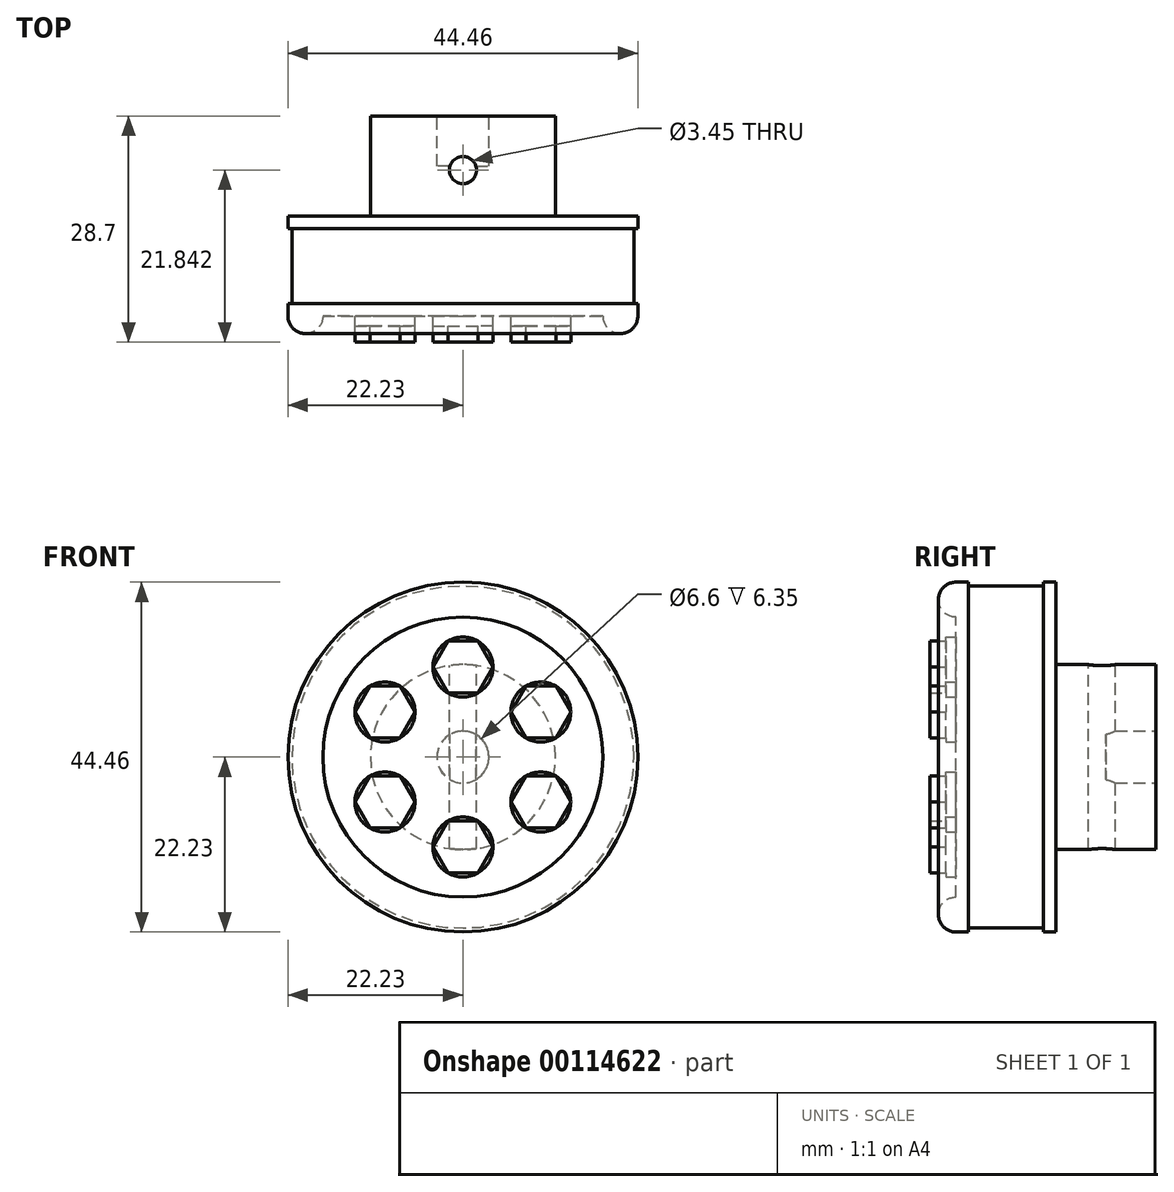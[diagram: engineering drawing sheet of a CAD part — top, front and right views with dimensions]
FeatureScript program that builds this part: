
annotation { "Feature Type Name" : "Feature", "Feature Type Description" : "" }
export const myFeature = defineFeature(function(context is Context, id is Id, definition is map)
    precondition{}
    {
        {
            var Q0;
            Q0=qCreatedBy(makeId("Front.planeOp"),FACE);
            var sketch = newSketch(context, id + "F0", { "sketchPlane" : qUnion([Q0])});
            skCircle(sketch, "E0", {"center": v(0, 0) * mm, "radius": 22.23 * mm});
            skSolve(sketch);
        }
        {
            var Q0;
            Q0 = qSketchRegion(id + "F0", true);
            extrude(context, id + "F1", {"entities" : qUnion([Q0]), "depth" : 12.7 * mm});
        }
        {
            var Q0;
            Q0=makeQuery(id+"F1.opExtrude","CAP_FACE",FACE,{"disambiguationData":[OSD([sQuery(id+"F0.wireOp",EDGE,"E0")])],"isStart":false});
            var sketch = newSketch(context, id + "F2", { "sketchPlane" : qUnion([Q0])});
            skLineSegment(sketch, "E1", {"start": v(0, 0) * mm, "end": v(0, 11.43) * mm, "construction": true});
            skCircle(sketch, "E2", {"center": v(0, 11.43) * mm, "radius": 3.81 * mm});
            skCircle(sketch, "E3.1.0", {"center": v(-9.9, 5.72) * mm, "radius": 3.81 * mm});
            skCircle(sketch, "E3.2.0", {"center": v(-9.9, -5.71) * mm, "radius": 3.81 * mm});
            skPoint(sketch, "E3.center", {"position": v(0, 0) * mm});
            skCircle(sketch, "E4.1.3.0", {"center": v(0, -11.43) * mm, "radius": 3.81 * mm});
            skCircle(sketch, "E4.1.4.0", {"center": v(9.9, -5.72) * mm, "radius": 3.81 * mm});
            skCircle(sketch, "E4.1.5.0", {"center": v(9.9, 5.72) * mm, "radius": 3.81 * mm});
            skLineSegment(sketch, "E5", {"start": v(0, 0) * mm, "end": v(-9.9, 5.72) * mm, "construction": true});
            skLineSegment(sketch, "E6", {"start": v(0, 0) * mm, "end": v(-22.23, 0) * mm, "construction": true});
            skSolve(sketch);
        }
        {
            var Q0;
            Q0 = qSketchRegion(id + "F2", true);
            extrude(context, id + "F3", {"entities" : qUnion([Q0]), "operationType" : NewBodyOperationType.ADD, "depth" : 1.27 * mm});
        }
        {
            var Q0;
            Q0=makeQuery(id+"F3.opExtrude","CAP_FACE",FACE,{"disambiguationData":[OSD([sQuery(id+"F2.wireOp",EDGE,"E2")])],"isStart":false});
            var sketch = newSketch(context, id + "F4", { "sketchPlane" : qUnion([Q0])});
            skLineSegment(sketch, "E7", {"start": v(0, 11.43) * mm, "end": v(3.81, 11.43) * mm, "construction": true});
            skCircle(sketch, "E8.cCircle", {"center": v(0, 11.43) * mm, "radius": 3.81 * mm, "construction": true});
            skLineSegment(sketch, "E8.0", {"start": v(3.81, 11.43) * mm, "end": v(1.9, 8.13) * mm});
            skLineSegment(sketch, "E8.1", {"start": v(1.9, 8.13) * mm, "end": v(-1.9, 8.13) * mm});
            skLineSegment(sketch, "E8.2", {"start": v(-1.9, 8.13) * mm, "end": v(-3.81, 11.43) * mm});
            skLineSegment(sketch, "E8.3", {"start": v(-3.81, 11.43) * mm, "end": v(-1.9, 14.73) * mm});
            skLineSegment(sketch, "E8.4", {"start": v(-1.9, 14.73) * mm, "end": v(1.9, 14.73) * mm});
            skLineSegment(sketch, "E8.5", {"start": v(1.9, 14.73) * mm, "end": v(3.81, 11.43) * mm});
            skLineSegment(sketch, "E9", {"start": v(0, 0) * mm, "end": v(-21.3, 0) * mm, "construction": true});
            skLineSegment(sketch, "E10", {"start": v(0, 0) * mm, "end": v(-9.62, 16.66) * mm, "construction": true});
            skLineSegment(sketch, "E11", {"start": v(0, 0) * mm, "end": v(9.66, 16.73) * mm, "construction": true});
            skLineSegment(sketch, "E12.MirrorCS", {"start": v(-6.09, 5.71) * mm, "end": v(-8, 9.01) * mm});
            skLineSegment(sketch, "E13.MirrorCS", {"start": v(-8, 2.42) * mm, "end": v(-6.09, 5.71) * mm});
            skLineSegment(sketch, "E14.MirrorCS", {"start": v(-11.8, 2.42) * mm, "end": v(-8, 2.42) * mm});
            skLineSegment(sketch, "E15.MirrorCS", {"start": v(-13.7, 5.71) * mm, "end": v(-11.8, 2.42) * mm});
            skLineSegment(sketch, "E16.MirrorCS", {"start": v(-11.8, 9.01) * mm, "end": v(-13.7, 5.71) * mm});
            skLineSegment(sketch, "E17.MirrorCS", {"start": v(-8, 9.01) * mm, "end": v(-11.8, 9.01) * mm});
            skLineSegment(sketch, "E18.MirrorCS", {"start": v(6.09, 5.72) * mm, "end": v(8, 2.42) * mm});
            skLineSegment(sketch, "E19.MirrorCS", {"start": v(8, 9.01) * mm, "end": v(6.09, 5.72) * mm});
            skLineSegment(sketch, "E20.MirrorCS", {"start": v(11.8, 9.01) * mm, "end": v(8, 9.01) * mm});
            skLineSegment(sketch, "E21.MirrorCS", {"start": v(13.7, 5.72) * mm, "end": v(11.8, 9.01) * mm});
            skLineSegment(sketch, "E22.MirrorCS", {"start": v(11.8, 2.42) * mm, "end": v(13.7, 5.72) * mm});
            skLineSegment(sketch, "E23.MirrorCS", {"start": v(8, 2.42) * mm, "end": v(11.8, 2.42) * mm});
            skLineSegment(sketch, "E24.MirrorCS", {"start": v(-11.8, -2.42) * mm, "end": v(-8, -2.42) * mm});
            skLineSegment(sketch, "E25.MirrorCS", {"start": v(-13.7, -5.71) * mm, "end": v(-11.8, -2.42) * mm});
            skLineSegment(sketch, "E26.MirrorCS", {"start": v(-11.8, -9.01) * mm, "end": v(-13.7, -5.71) * mm});
            skLineSegment(sketch, "E27.MirrorCS", {"start": v(-8, -9.01) * mm, "end": v(-11.8, -9.01) * mm});
            skLineSegment(sketch, "E28.MirrorCS", {"start": v(-6.09, -5.71) * mm, "end": v(-8, -9.01) * mm});
            skLineSegment(sketch, "E29.MirrorCS", {"start": v(-8, -2.42) * mm, "end": v(-6.09, -5.71) * mm});
            skLineSegment(sketch, "E30.MirrorCS", {"start": v(1.9, -8.13) * mm, "end": v(-1.9, -8.13) * mm});
            skLineSegment(sketch, "E31.MirrorCS", {"start": v(3.81, -11.43) * mm, "end": v(1.9, -8.13) * mm});
            skLineSegment(sketch, "E32.MirrorCS", {"start": v(1.9, -14.73) * mm, "end": v(3.81, -11.43) * mm});
            skLineSegment(sketch, "E33.MirrorCS", {"start": v(-1.9, -14.73) * mm, "end": v(1.9, -14.73) * mm});
            skLineSegment(sketch, "E34.MirrorCS", {"start": v(-3.81, -11.43) * mm, "end": v(-1.9, -14.73) * mm});
            skLineSegment(sketch, "E35.MirrorCS", {"start": v(-1.9, -8.13) * mm, "end": v(-3.81, -11.43) * mm});
            skLineSegment(sketch, "E36.MirrorCS", {"start": v(6.09, -5.72) * mm, "end": v(8, -2.42) * mm});
            skLineSegment(sketch, "E37.MirrorCS", {"start": v(8, -9.01) * mm, "end": v(6.09, -5.72) * mm});
            skLineSegment(sketch, "E38.MirrorCS", {"start": v(11.8, -9.01) * mm, "end": v(8, -9.01) * mm});
            skLineSegment(sketch, "E39.MirrorCS", {"start": v(13.7, -5.72) * mm, "end": v(11.8, -9.01) * mm});
            skLineSegment(sketch, "E40.MirrorCS", {"start": v(11.8, -2.42) * mm, "end": v(13.7, -5.72) * mm});
            skLineSegment(sketch, "E41.MirrorCS", {"start": v(8, -2.42) * mm, "end": v(11.8, -2.42) * mm});
            skSolve(sketch);
        }
        {
            var Q0;
            Q0 = qSketchRegion(id + "F4", true);
            extrude(context, id + "F5", {"entities" : qUnion([Q0]), "operationType" : NewBodyOperationType.ADD, "depth" : 2.03 * mm});
        }
        {
            var Q0;
            Q0=makeQuery(id+"F1.opExtrude","CAP_FACE",FACE,{"disambiguationData":[OSD([sQuery(id+"F0.wireOp",EDGE,"E0")])],"isStart":false});
            var sketch = newSketch(context, id + "F6", { "sketchPlane" : qUnion([Q0])});
            skCircle(sketch, "E42", {"center": v(0, 0) * mm, "radius": 17.78 * mm});
            skCircle(sketch, "E43", {"center": v(0, 0) * mm, "radius": 22.23 * mm});
            skPoint(sketch, "E44", {"position": v(0, 17.78) * mm});
            skPoint(sketch, "E45", {"position": v(0, 22.23) * mm});
            skSolve(sketch);
        }
        {
            var Q0;
            Q0 = qSketchRegion(id + "F6", true);
            extrude(context, id + "F7", {"entities" : qUnion([Q0]), "operationType" : NewBodyOperationType.ADD, "depth" : 2.22 * mm});
        }
        {
            var Q0;
            Q0=makeQuery(id+"F7.opExtrude","CAP_EDGE",EDGE,{"disambiguationData":[OSD([sQuery(id+"F6.wireOp",EDGE,"E42")])],"isStart":false});
            fillet(context, id + "F8", {"entities" : qUnion([Q0]), "radius" : 2.22 * mm, "tangentPropagation" : true, "allowEdgeOverflow" : false});
        }
        {
            var Q0;
            Q0=makeQuery(id+"F7.opExtrude","CAP_EDGE",EDGE,{"disambiguationData":[OSD([sQuery(id+"F6.wireOp",EDGE,"E43")])],"isStart":false});
            fillet(context, id + "F9", {"entities" : qUnion([Q0]), "radius" : 2.22 * mm, "tangentPropagation" : true, "allowEdgeOverflow" : false});
        }
        {
            var Q0;
            Q0=makeQuery(id+"F1.opExtrude","CAP_FACE",FACE,{"disambiguationData":[OSD([sQuery(id+"F0.wireOp",EDGE,"E0")])],"isStart":true});
            var sketch = newSketch(context, id + "F10", { "sketchPlane" : qUnion([Q0])});
            skCircle(sketch, "E46", {"center": v(0, 0) * mm, "radius": 11.75 * mm});
            skSolve(sketch);
        }
        {
            var Q0;
            Q0 = qSketchRegion(id + "F10", true);
            extrude(context, id + "F11", {"entities" : qUnion([Q0]), "operationType" : NewBodyOperationType.ADD, "depth" : 12.7 * mm});
        }
        {
            var Q0;
            Q0=makeQuery(id+"F11.opExtrude","CAP_FACE",FACE,{"disambiguationData":[OSD([sQuery(id+"F10.wireOp",EDGE,"E46")])],"isStart":false});
            var sketch = newSketch(context, id + "F12", { "sketchPlane" : qUnion([Q0])});
            skCircle(sketch, "E47", {"center": v(0, 0) * mm, "radius": 3.3 * mm});
            skSolve(sketch);
        }
        {
            var Q0;
            Q0 = qSketchRegion(id + "F12", true);
            extrude(context, id + "F13", {"entities" : qUnion([Q0]), "operationType" : NewBodyOperationType.REMOVE, "oppositeDirection" : true, "depth" : 6.35 * mm});
        }
        {
            var Q0;
            Q0=qCreatedBy(makeId("Top.planeOp"),FACE);
            var sketch = newSketch(context, id + "F14", { "sketchPlane" : qUnion([Q0])});
            skLineSegment(sketch, "E48.0", {"start": v(-11.75, 12.7) * mm, "end": v(11.75, 12.7) * mm});
            skLineSegment(sketch, "E49", {"start": v(-11.75, 12.7) * mm, "end": v(11.75, 12.7) * mm, "construction": true});
            skPoint(sketch, "E50", {"position": v(0, 12.7) * mm});
            skLineSegment(sketch, "E51", {"start": v(0, 12.7) * mm, "end": v(0, 5.84) * mm, "construction": true});
            skCircle(sketch, "E52", {"center": v(0, 5.84) * mm, "radius": 1.73 * mm});
            skSolve(sketch);
        }
        {
            var Q0;
            Q0 = qSketchRegion(id + "F14", true);
            extrude(context, id + "F15", {"entities" : qUnion([Q0]), "operationType" : NewBodyOperationType.REMOVE, "endBound" : BoundingType.SYMMETRIC, "oppositeDirection" : true, "depth" : 127 * mm});
        }
        {
            var Q0;
            Q0=qCreatedBy(makeId("Right.planeOp"),FACE);
            var sketch = newSketch(context, id + "F16", { "sketchPlane" : qUnion([Q0])});
            skLineSegment(sketch, "E53", {"start": v(-12.7, 22.23) * mm, "end": v(0, 22.23) * mm});
            skLineSegment(sketch, "E54.bottom", {"start": v(-11.11, 22.73) * mm, "end": v(-1.59, 22.73) * mm});
            skLineSegment(sketch, "E54.top", {"start": v(-11.11, 21.72) * mm, "end": v(-1.59, 21.72) * mm});
            skLineSegment(sketch, "E54.left", {"start": v(-11.11, 22.73) * mm, "end": v(-11.11, 21.72) * mm});
            skLineSegment(sketch, "E54.right", {"start": v(-1.59, 22.73) * mm, "end": v(-1.59, 21.72) * mm});
            skPoint(sketch, "E54.middle", {"position": v(-6.35, 22.23) * mm});
            skSolve(sketch);
        }
        {
            var Q0;
            Q0=qCreatedBy(makeId("Right.planeOp"),FACE);
            var sketch = newSketch(context, id + "F17", { "sketchPlane" : qUnion([Q0])});
            skLineSegment(sketch, "E55", {"start": v(0, 0) * mm, "end": v(23.4, 0) * mm, "construction": true});
            skSolve(sketch);
        }
        {
            var Q0;
            Q0 = qSketchRegion(id + "F16", true);
            var Q1;
            Q1=sQuery(id+"F17.wireOp",EDGE,"E55");
            revolve(context, id + "F18", {"operationType" : NewBodyOperationType.REMOVE, "entities" : qUnion([Q0]), "axis" : qUnion([Q1]), "revolveType" : RevolveType.FULL, "oppositeDirection" : true});
        }
    });
